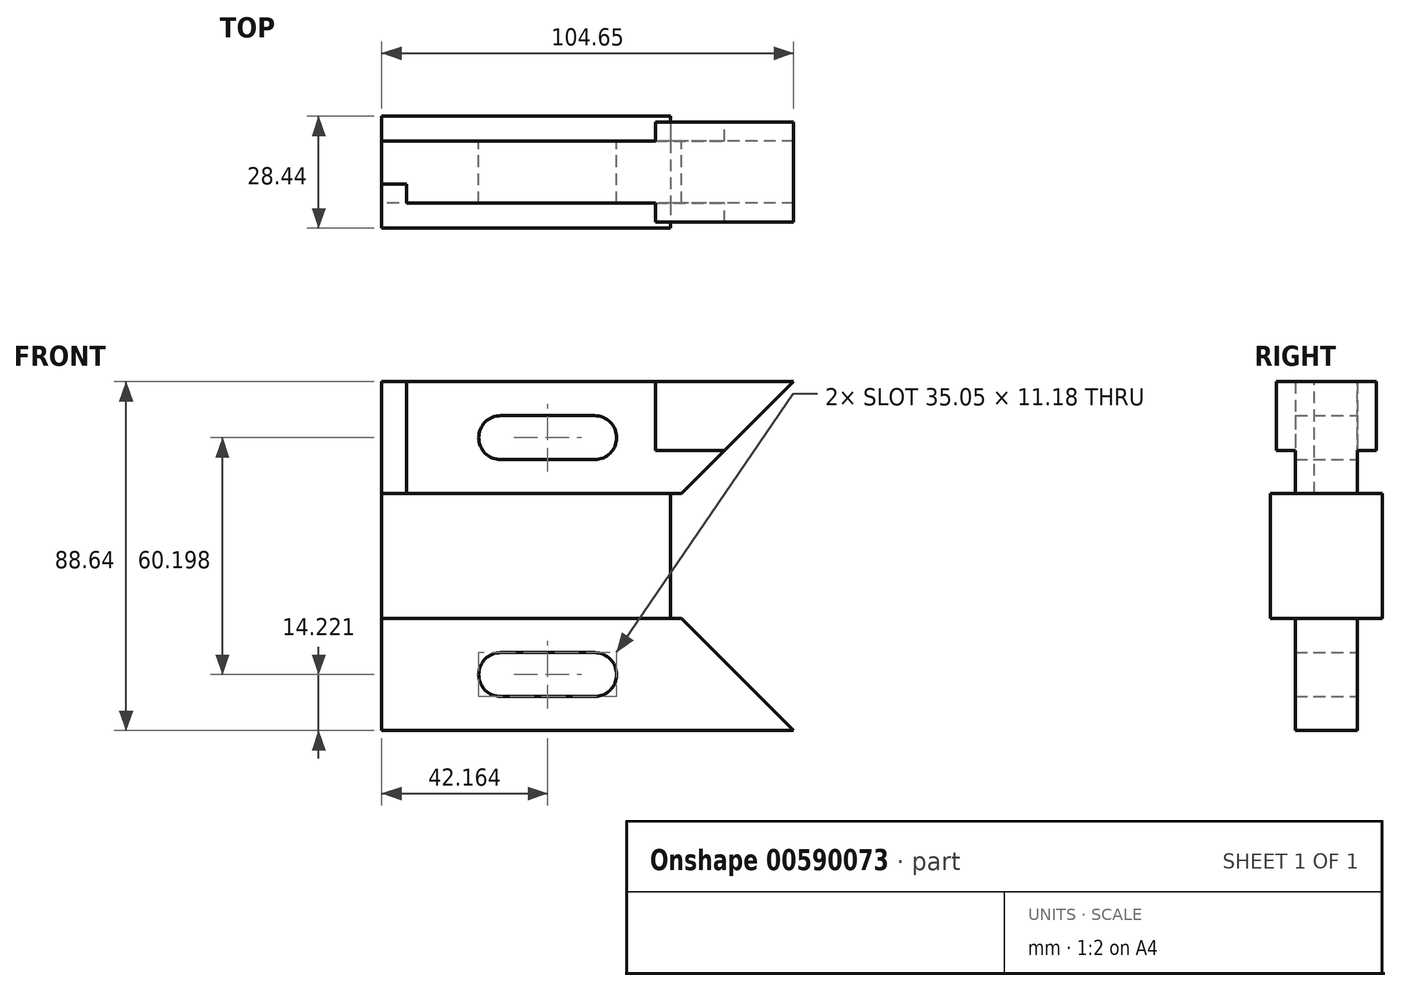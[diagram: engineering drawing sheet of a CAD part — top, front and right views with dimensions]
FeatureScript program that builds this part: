
annotation { "Feature Type Name" : "Feature", "Feature Type Description" : "" }
export const myFeature = defineFeature(function(context is Context, id is Id, definition is map)
    precondition{}
    {
        {
            var Q0;
            Q0=qCreatedBy(makeId("Right.planeOp"),FACE);
            var sketch = newSketch(context, id + "F0", { "sketchPlane" : qUnion([Q0])});
            skLineSegment(sketch, "E0.bottom", {"start": v(14.22, -15.87) * mm, "end": v(-14.22, -15.88) * mm});
            skLineSegment(sketch, "E0.top", {"start": v(14.22, 15.88) * mm, "end": v(-14.22, 15.88) * mm});
            skLineSegment(sketch, "E0.left", {"start": v(14.22, -15.88) * mm, "end": v(14.22, 15.88) * mm});
            skLineSegment(sketch, "E0.right", {"start": v(-14.22, -15.88) * mm, "end": v(-14.22, 15.88) * mm});
            skPoint(sketch, "E0.middle", {"position": v(0, 0) * mm});
            skSolve(sketch);
        }
        {
            var Q0;
            Q0=qSketchRegion(id+"F0",true);
            extrude(context, id + "F1", {"entities" : qUnion([Q0]), "depth" : 73.4 * mm, "offsetDistance" : 25.4 * mm});
        }
        {
            var Q0;
            Q0=qCreatedBy(makeId("Front.planeOp"),FACE);
            var sketch = newSketch(context, id + "F2", { "sketchPlane" : qUnion([Q0])});
            skLineSegment(sketch, "E1.0", {"start": v(73.4, 15.88) * mm, "end": v(0, 15.88) * mm});
            skLineSegment(sketch, "E2", {"start": v(0, 15.88) * mm, "end": v(0, 44.32) * mm});
            skLineSegment(sketch, "E3", {"start": v(0, 44.32) * mm, "end": v(104.65, 44.32) * mm});
            skLineSegment(sketch, "E4", {"start": v(104.65, 44.32) * mm, "end": v(76.2, 15.87) * mm});
            skLineSegment(sketch, "E5", {"start": v(76.2, 15.88) * mm, "end": v(73.4, 15.88) * mm});
            skCircle(sketch, "E6", {"center": v(30.23, 30.1) * mm, "radius": 5.59 * mm});
            skCircle(sketch, "E7", {"center": v(54.1, 30.1) * mm, "radius": 5.59 * mm});
            skLineSegment(sketch, "E8", {"start": v(30.23, 35.69) * mm, "end": v(54.1, 35.69) * mm});
            skLineSegment(sketch, "E9", {"start": v(30.23, 24.51) * mm, "end": v(54.1, 24.51) * mm});
            skLineSegment(sketch, "E10.MirrorCS", {"start": v(76.2, -15.88) * mm, "end": v(73.4, -15.88) * mm});
            skLineSegment(sketch, "E11.MirrorCS", {"start": v(104.65, -44.32) * mm, "end": v(76.2, -15.87) * mm});
            skLineSegment(sketch, "E12.MirrorCS", {"start": v(30.23, -24.51) * mm, "end": v(54.1, -24.51) * mm});
            skCircle(sketch, "E13.MirrorC", {"center": v(30.23, -30.1) * mm, "radius": 5.59 * mm});
            skLineSegment(sketch, "E14.MirrorCS", {"start": v(0, -44.32) * mm, "end": v(104.65, -44.32) * mm});
            skLineSegment(sketch, "E15.MirrorCS", {"start": v(73.4, -15.88) * mm, "end": v(0, -15.88) * mm});
            skLineSegment(sketch, "E16.MirrorCS", {"start": v(0, -15.88) * mm, "end": v(0, -44.32) * mm});
            skLineSegment(sketch, "E17.MirrorCS", {"start": v(30.23, -35.69) * mm, "end": v(54.1, -35.69) * mm});
            skCircle(sketch, "E18.MirrorC", {"center": v(54.1, -30.1) * mm, "radius": 5.59 * mm});
            skSolve(sketch);
        }
        {
            var Q0;
            Q0=qSketchRegion(id+"F2",true);
            extrude(context, id + "F3", {"entities" : qUnion([Q0]), "operationType" : NewBodyOperationType.ADD, "depth" : 15.75 * mm, "offsetDistance" : 25.4 * mm, "symmetric" : true});
        }
        {
            var Q0;
            Q0=makeQuery(id+"F3.opExtrude","CAP_FACE",FACE,{"disambiguationData":[OSD([sQuery(id+"F2.wireOp",EDGE,"E3"),sQuery(id+"F2.wireOp",EDGE,"E6"),sQuery(id+"F2.wireOp",EDGE,"E7"),sQuery(id+"F2.wireOp",EDGE,"E8"),sQuery(id+"F2.wireOp",EDGE,"E9"),sQuery(id+"F2.wireOp",EDGE,"E2"),sQuery(id+"F2.wireOp",EDGE,"E5"),sQuery(id+"F2.wireOp",EDGE,"E1.0"),sQuery(id+"F2.wireOp",EDGE,"E4")])],"isStart":false});
            var sketch = newSketch(context, id + "F4", { "sketchPlane" : qUnion([Q0])});
            skLineSegment(sketch, "E19.bottom", {"start": v(0, 44.32) * mm, "end": v(6.35, 44.32) * mm});
            skLineSegment(sketch, "E19.top", {"start": v(0, 15.88) * mm, "end": v(6.35, 15.88) * mm});
            skLineSegment(sketch, "E19.left", {"start": v(0, 44.32) * mm, "end": v(0, 15.88) * mm});
            skLineSegment(sketch, "E19.right", {"start": v(6.35, 44.32) * mm, "end": v(6.35, 15.88) * mm});
            skLineSegment(sketch, "E20", {"start": v(87.12, 26.8) * mm, "end": v(69.6, 26.8) * mm});
            skLineSegment(sketch, "E21", {"start": v(69.6, 26.8) * mm, "end": v(69.6, 44.32) * mm});
            skSolve(sketch);
        }
        {
            var Q0;
            Q0=qSketchRegion(id+"F4",true);
            extrude(context, id + "F5", {"entities" : qUnion([Q0]), "operationType" : NewBodyOperationType.REMOVE, "oppositeDirection" : true, "depth" : 4.83 * mm, "offsetDistance" : 25.4 * mm});
        }
        {
            var Q0;
            {var subQ0=sQuery(id+"F4.wireOp",EDGE,"E20");Q0=makeQuery(id+"F4.imprint","IMPRINT",FACE,{"disambiguationData":[TD([[makeQuery(id+"F4.imprint","IMPRINT",EDGE,{"derivedFrom":subQ0}),-1.0]])]});}
            extrude(context, id + "F6", {"entities" : qUnion([Q0]), "operationType" : NewBodyOperationType.ADD, "depth" : 4.83 * mm, "offsetDistance" : 25.4 * mm, "hasSecondDirection" : true, "secondDirectionOppositeDirection" : true, "secondDirectionDepth" : 20.57 * mm});
        }
    });
